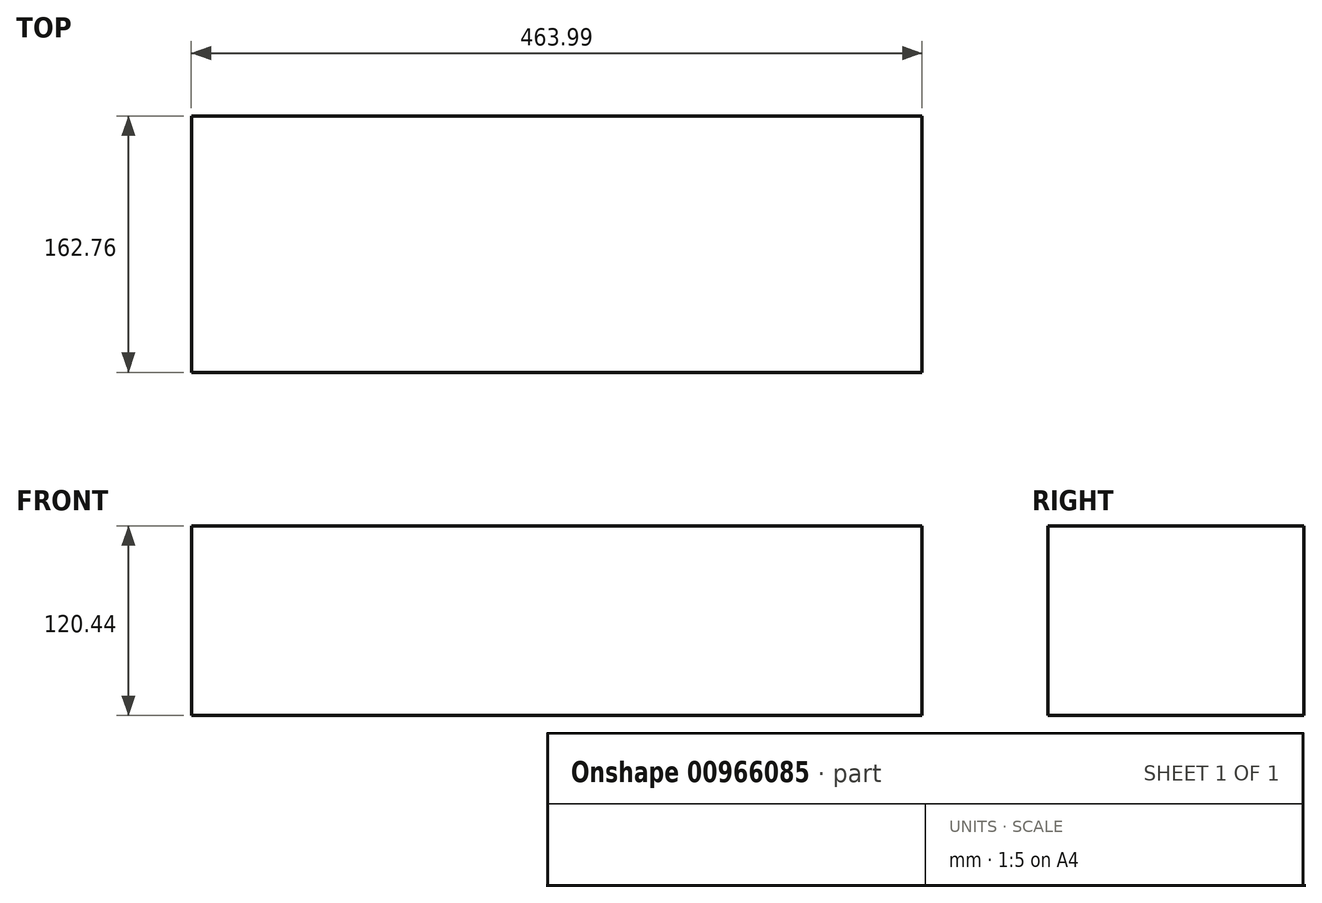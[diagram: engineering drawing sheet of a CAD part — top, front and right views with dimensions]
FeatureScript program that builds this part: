
annotation { "Feature Type Name" : "Feature", "Feature Type Description" : "" }
export const myFeature = defineFeature(function(context is Context, id is Id, definition is map)
    precondition{}
    {
        {
            var Q0;
            Q0=qCreatedBy(makeId("Top.planeOp"),FACE);
            var sketch = newSketch(context, id + "F0", { "sketchPlane" : qUnion([Q0])});
            skLineSegment(sketch, "E0.bottom", {"start": v(118.65, 324.77) * mm, "end": v(-124.88, 324.77) * mm});
            skLineSegment(sketch, "E0.top", {"start": v(118.65, 162.01) * mm, "end": v(-124.88, 162.01) * mm});
            skLineSegment(sketch, "E0.left", {"start": v(118.65, 324.77) * mm, "end": v(118.65, 162.01) * mm});
            skLineSegment(sketch, "E0.right", {"start": v(-124.88, 324.77) * mm, "end": v(-124.88, 162.01) * mm});
            skSolve(sketch);
        }
        {
            var Q0;
            Q0=makeQuery(id+"F0.imprint","IMPRINT",FACE,{"disambiguationData":[TD([[makeQuery(id+"F0.imprint","IMPRINT",EDGE,{"derivedFrom":sQuery(id+"F0.wireOp",EDGE,"E0.bottom")}),1.0]])]});
            extrude(context, id + "F1", {"entities" : qUnion([Q0]), "depth" : 120.44 * mm, "offsetDistance" : 25.4 * mm});
        }
        {
            var Q0;
            Q0=makeQuery(id+"F1.opExtrude","SWEPT_FACE",FACE,{"disambiguationData":[OSD([sQuery(id+"F0.wireOp",EDGE,"E0.left")])]});
            var sketch = newSketch(context, id + "F2", { "sketchPlane" : qUnion([Q0])});
            skSolve(sketch);
        }
        {
            var Q0;
            {var subQ0=sQuery(id+"F0.wireOp",EDGE,"E0.left");Q0=makeQuery(id+"F2.imprint","IMPRINT",FACE,{"disambiguationData":[TD([[makeQuery(id+"F2.imprint","IMPRINT",EDGE,{"derivedFrom":makeQuery(id+"F1.opExtrude","CAP_EDGE",EDGE,{"disambiguationData":[OSD([subQ0])],"isStart":true})}),-1.0]])]});}
            extrude(context, id + "F3", {"entities" : qUnion([Q0]), "operationType" : NewBodyOperationType.ADD, "depth" : 220.46 * mm, "offsetDistance" : 25.4 * mm});
        }
    });
